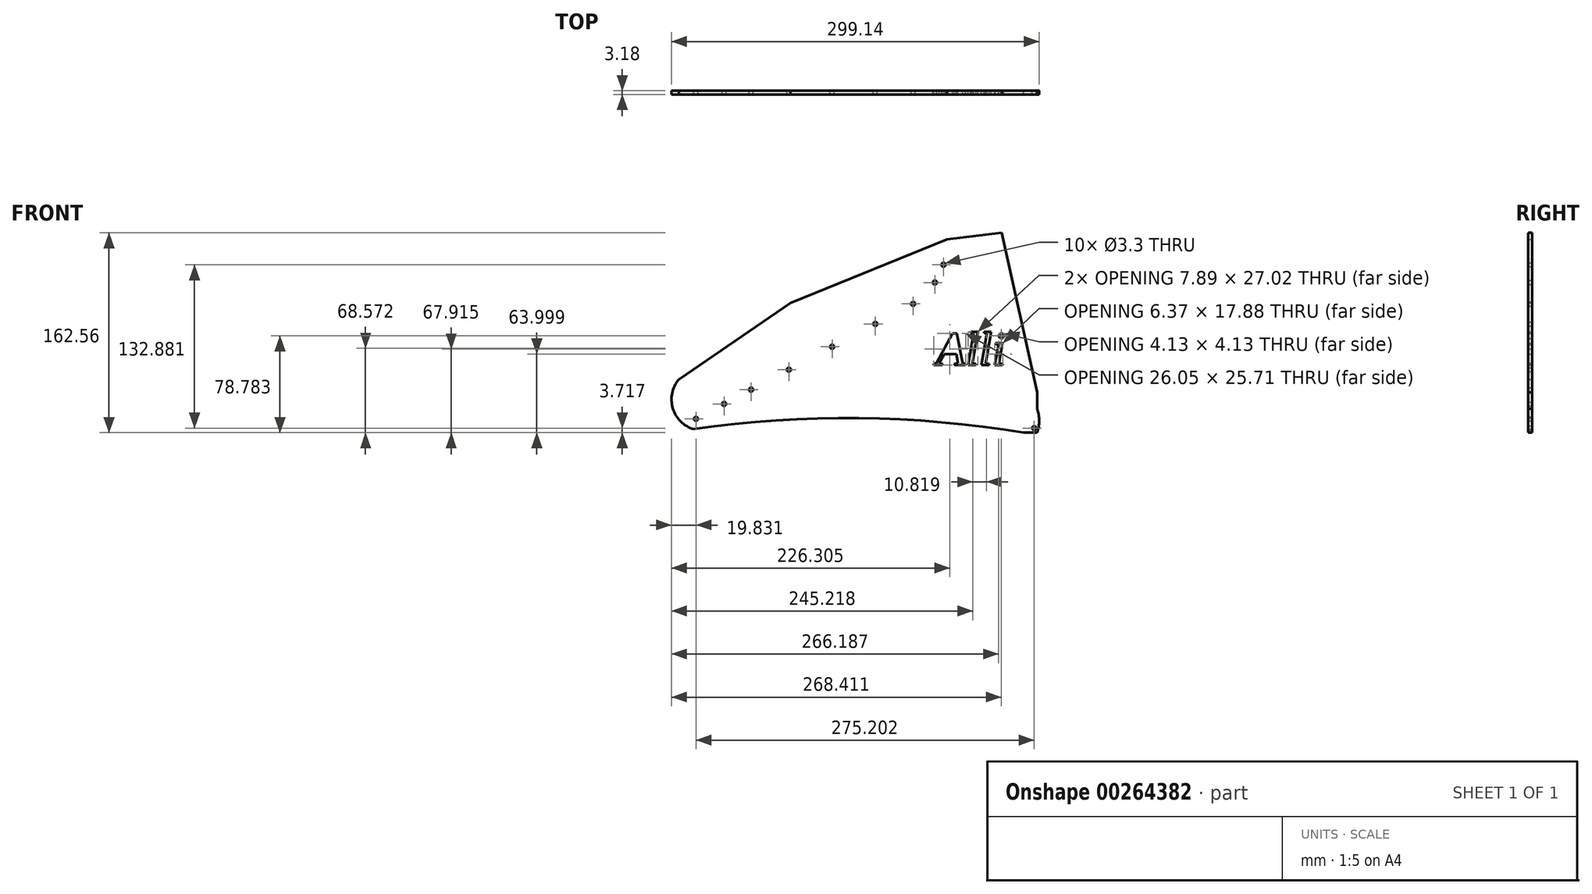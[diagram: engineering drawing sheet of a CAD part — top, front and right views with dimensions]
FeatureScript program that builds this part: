
annotation { "Feature Type Name" : "Feature", "Feature Type Description" : "" }
export const myFeature = defineFeature(function(context is Context, id is Id, definition is map)
    precondition{}
    {
        {
            var Q0;
            Q0=qCreatedBy(makeId("Front.planeOp"),FACE);
            var sketch = newSketch(context, id + "F0", { "sketchPlane" : qUnion([Q0])});
            skCircle(sketch, "E0", {"center": v(-123.68, -81.3) * mm, "radius": 1.65 * mm});
            skCircle(sketch, "E1", {"center": v(-57.79, -46.44) * mm, "radius": 1.65 * mm});
            skCircle(sketch, "E2", {"center": v(-145.66, -92.94) * mm, "radius": 1.65 * mm});
            skCircle(sketch, "E3", {"center": v(-168.58, -105.07) * mm, "radius": 1.65 * mm});
            skCircle(sketch, "E4", {"center": v(-92.94, -65.05) * mm, "radius": 1.65 * mm});
            skCircle(sketch, "E5", {"center": v(-22.63, -27.84) * mm, "radius": 1.65 * mm});
            skCircle(sketch, "E6", {"center": v(8.1, -11.58) * mm, "radius": 1.65 * mm});
            skCircle(sketch, "E7", {"center": v(25.82, 5.87) * mm, "radius": 1.65 * mm});
            skCircle(sketch, "E8", {"center": v(32.85, 20.28) * mm, "radius": 1.65 * mm});
            skArc(sketch, "E9", {"start": v(-182.55, -73.1) * mm, "mid": v(-187.35, -96.5) * mm, "end": v(-170.47, -113.42) * mm});
            skLineSegment(sketch, "E10", {"start": v(-182.55, -73.1) * mm, "end": v(-91.72, -10.65) * mm});
            skLineSegment(sketch, "E11", {"start": v(-91.72, -10.65) * mm, "end": v(35.83, 41.04) * mm});
            skText(sketch, "E12", { "text": "Alli", "fontName": "Tinos-Italic.ttf"});
            skLineSegment(sketch, "E13", {"start": v(98.02, -116.32) * mm, "end": v(108.93, -116.32) * mm});
            skCircle(sketch, "E14", {"center": v(106.62, -112.6) * mm, "radius": 1.65 * mm});
            skArc(sketch, "E15", {"start": v(108.93, -116.32) * mm, "mid": v(110.73, -106.61) * mm, "end": v(108.93, -96.9) * mm});
            skLineSegment(sketch, "E16", {"start": v(35.83, 41.04) * mm, "end": v(80.27, 46.24) * mm});
            skLineSegment(sketch, "E17", {"start": v(108.93, -96.9) * mm, "end": v(108.93, -83.34) * mm});
            skLineSegment(sketch, "E18", {"start": v(80.27, 46.24) * mm, "end": v(108.93, -83.34) * mm});
            skArc(sketch, "E19", {"start": v(98.02, -116.32) * mm, "mid": v(-36.1, -104.5) * mm, "end": v(-170.47, -113.42) * mm});
            const initialGuessF0  = {"E12": [0.027, -0.06126, 1, 0, 0.02804]};
            skSetInitialGuess(sketch, initialGuessF0);
            skSolve(sketch);
        }
        {
            var Q0;
            Q0 = qSketchRegion(id + "F0", true);
            extrude(context, id + "F1", {"entities" : qUnion([Q0]), "depth" : 3.17 * mm});
        }
    });
